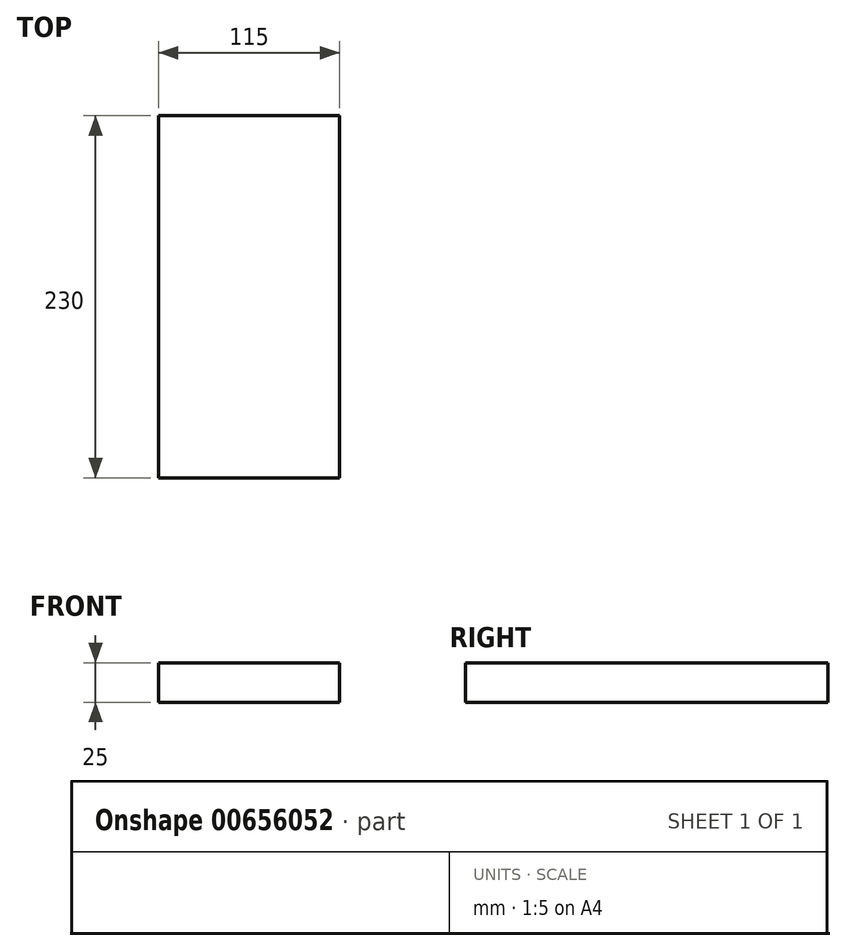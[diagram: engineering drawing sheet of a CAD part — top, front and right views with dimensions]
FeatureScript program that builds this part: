
annotation { "Feature Type Name" : "Feature", "Feature Type Description" : "" }
export const myFeature = defineFeature(function(context is Context, id is Id, definition is map)
    precondition{}
    {
        {
            var Q0;
            Q0=qCreatedBy(makeId("Front.planeOp"),FACE);
            var sketch = newSketch(context, id + "F0", { "sketchPlane" : qUnion([Q0])});
            skLineSegment(sketch, "E0.bottom", {"start": v(0, 0) * mm, "end": v(115, 0) * mm});
            skLineSegment(sketch, "E0.top", {"start": v(0, 25) * mm, "end": v(115, 25) * mm});
            skLineSegment(sketch, "E0.left", {"start": v(0, 0) * mm, "end": v(0, 25) * mm});
            skLineSegment(sketch, "E0.right", {"start": v(115, 0) * mm, "end": v(115, 25) * mm});
            skSolve(sketch);
        }
        {
            var Q0;
            Q0=makeQuery(id+"F0.imprint","IMPRINT",FACE,{"disambiguationData":[TD([[makeQuery(id+"F0.imprint","IMPRINT",EDGE,{"derivedFrom":sQuery(id+"F0.wireOp",EDGE,"E0.bottom")}),1.0]])]});
            extrude(context, id + "F1", {"entities" : qUnion([Q0]), "depth" : 230 * mm, "offsetDistance" : 25.4 * mm});
        }
    });
